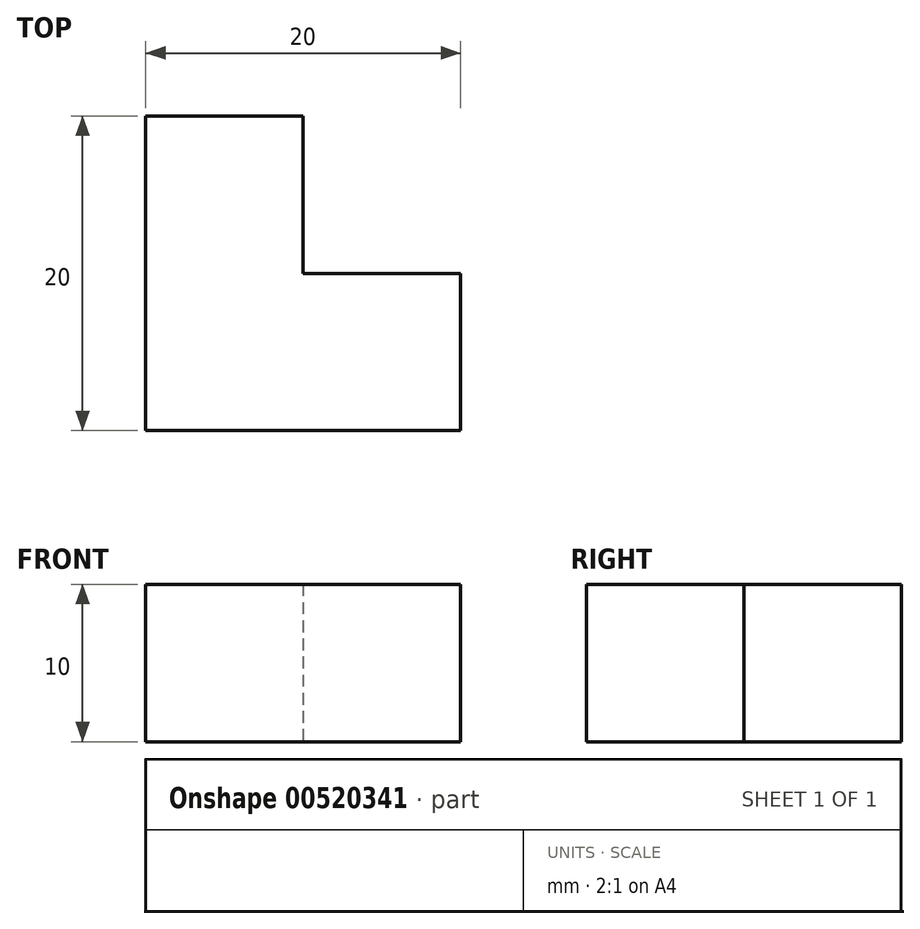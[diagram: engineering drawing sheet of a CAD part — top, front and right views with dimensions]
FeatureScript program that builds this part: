
annotation { "Feature Type Name" : "Feature", "Feature Type Description" : "" }
export const myFeature = defineFeature(function(context is Context, id is Id, definition is map)
    precondition{}
    {
        {
            var Q0;
            Q0=qCreatedBy(makeId("Top.planeOp"),FACE);
            var sketch = newSketch(context, id + "F0", { "sketchPlane" : qUnion([Q0])});
            skLineSegment(sketch, "E0", {"start": v(6.05, 0) * mm, "end": v(6.05, 20) * mm});
            skLineSegment(sketch, "E1", {"start": v(6.05, 20) * mm, "end": v(16.05, 20) * mm});
            skLineSegment(sketch, "E2", {"start": v(16.05, 20) * mm, "end": v(16.05, 10) * mm});
            skLineSegment(sketch, "E3", {"start": v(16.05, 10) * mm, "end": v(26.05, 10) * mm});
            skLineSegment(sketch, "E4", {"start": v(26.05, 10) * mm, "end": v(26.05, 0) * mm});
            skLineSegment(sketch, "E5", {"start": v(26.05, 0) * mm, "end": v(6.05, 0) * mm});
            skSolve(sketch);
        }
        {
            var Q0;
            Q0=makeQuery(id+"F0.imprint","IMPRINT",FACE,{"disambiguationData":[TD([[makeQuery(id+"F0.imprint","IMPRINT",EDGE,{"derivedFrom":sQuery(id+"F0.wireOp",EDGE,"E0")}),-1.0]])]});
            extrude(context, id + "F1", {"entities" : qUnion([Q0]), "depth" : 10 * mm, "offsetDistance" : 25 * mm});
        }
    });
